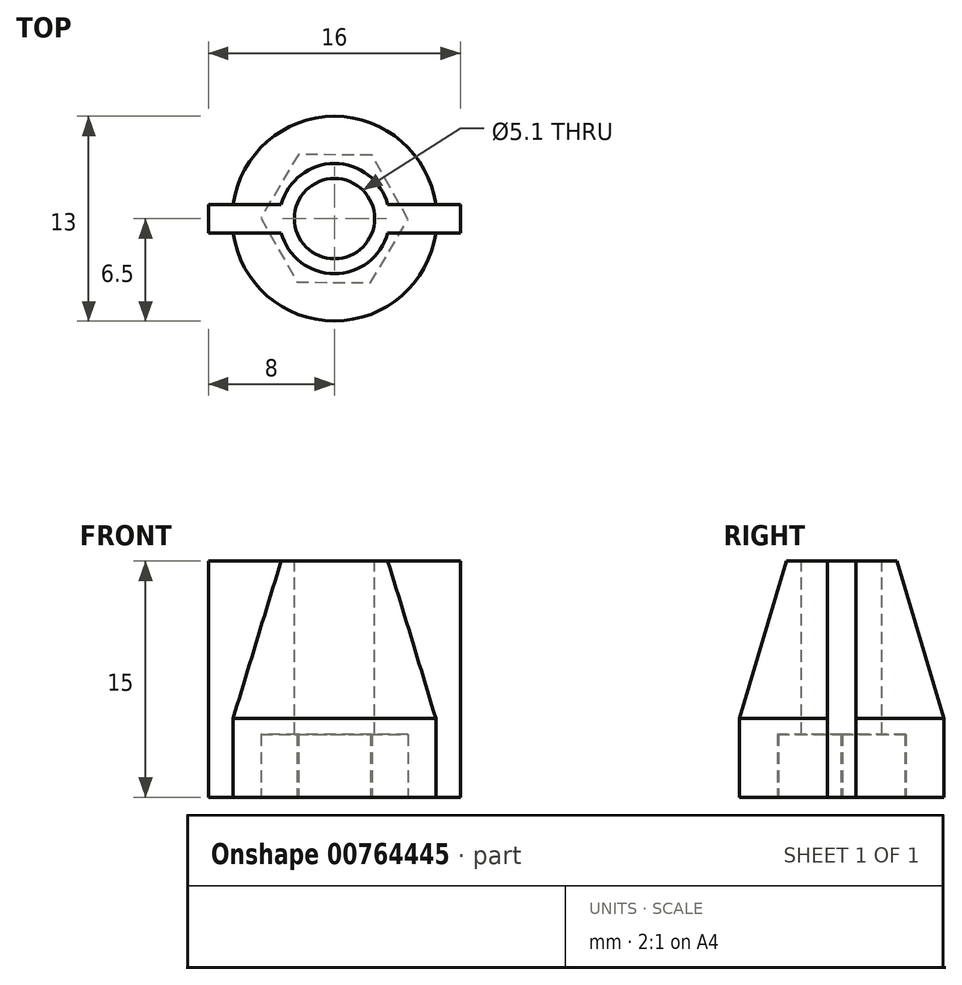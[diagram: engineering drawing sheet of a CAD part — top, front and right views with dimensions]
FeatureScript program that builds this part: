
annotation { "Feature Type Name" : "Feature", "Feature Type Description" : "" }
export const myFeature = defineFeature(function(context is Context, id is Id, definition is map)
    precondition{}
    {
        {
            var Q0;
            Q0=qCreatedBy(makeId("Top.planeOp"),FACE);
            var sketch = newSketch(context, id + "F0", { "sketchPlane" : qUnion([Q0])});
            skCircle(sketch, "E0", {"center": v(0, 0) * mm, "radius": 6.5 * mm});
            skSolve(sketch);
        }
        {
            var Q0;
            Q0 = qSketchRegion(id + "F0", true);
            extrude(context, id + "F1", {"entities" : qUnion([Q0]), "depth" : 15 * mm, "offsetDistance" : 25 * mm});
        }
        {
            var Q0;
            Q0=makeQuery(id+"F1.opExtrude","CAP_EDGE",EDGE,{"disambiguationData":[OSD([sQuery(id+"F0.wireOp",EDGE,"E0")])],"isStart":false});
            chamfer(context, id + "F2", {"entities" : qUnion([Q0]), "chamferType" : ChamferType.TWO_OFFSETS, "width1" : 3 * mm, "oppositeDirection" : false, "width2" : 10 * mm, "tangentPropagation" : true});
        }
        {
            var Q0;
            Q0=makeQuery(id+"F1.opExtrude","CAP_FACE",FACE,{"disambiguationData":[OSD([sQuery(id+"F0.wireOp",EDGE,"E0")])],"isStart":false});
            var sketch = newSketch(context, id + "F3", { "sketchPlane" : qUnion([Q0])});
            skLineSegment(sketch, "E1.bottom", {"start": v(8, 0.9) * mm, "end": v(-8, 0.9) * mm});
            skLineSegment(sketch, "E1.top", {"start": v(8, -0.9) * mm, "end": v(-8, -0.9) * mm});
            skLineSegment(sketch, "E1.left", {"start": v(8, 0.9) * mm, "end": v(8, -0.9) * mm});
            skLineSegment(sketch, "E1.right", {"start": v(-8, 0.9) * mm, "end": v(-8, -0.9) * mm});
            skPoint(sketch, "E1.middle", {"position": v(0, 0) * mm});
            skSolve(sketch);
        }
        {
            var Q0;
            Q0 = qSketchRegion(id + "F3", true);
            extrude(context, id + "F4", {"entities" : qUnion([Q0]), "operationType" : NewBodyOperationType.ADD, "oppositeDirection" : true, "depth" : 15 * mm, "offsetDistance" : 25 * mm});
        }
        {
            var Q0;
            Q0=makeQuery(id+"F4.boolean.opBoolean","MERGE",FACE,{"derivedFrom":[makeQuery(id+"F1.opExtrude","CAP_FACE",FACE,{"disambiguationData":[OSD([sQuery(id+"F0.wireOp",EDGE,"E0")])],"isStart":true}),makeQuery(id+"F4.opExtrude","CAP_FACE",FACE,{"disambiguationData":[OSD([sQuery(id+"F3.wireOp",EDGE,"E1.bottom"),sQuery(id+"F3.wireOp",EDGE,"E1.top"),sQuery(id+"F3.wireOp",EDGE,"E1.left"),sQuery(id+"F3.wireOp",EDGE,"E1.right")])],"isStart":false})]});
            var sketch = newSketch(context, id + "F5", { "sketchPlane" : qUnion([Q0])});
            skCircle(sketch, "E2.cCircle", {"center": v(0, 0) * mm, "radius": 4.05 * mm, "construction": true});
            skLineSegment(sketch, "E2.0", {"start": v(4.68, 0.05) * mm, "end": v(2.38, -4.03) * mm});
            skLineSegment(sketch, "E2.1", {"start": v(2.38, -4.03) * mm, "end": v(-2.3, -4.07) * mm});
            skLineSegment(sketch, "E2.2", {"start": v(-2.3, -4.07) * mm, "end": v(-4.68, -0.05) * mm});
            skLineSegment(sketch, "E2.3", {"start": v(-4.68, -0.05) * mm, "end": v(-2.38, 4.03) * mm});
            skLineSegment(sketch, "E2.4", {"start": v(-2.38, 4.03) * mm, "end": v(2.3, 4.07) * mm});
            skLineSegment(sketch, "E2.5", {"start": v(2.3, 4.07) * mm, "end": v(4.68, 0.05) * mm});
            skPoint(sketch, "E2.0.midPoint", {"position": v(3.53, -1.99) * mm});
            skSolve(sketch);
        }
        {
            var Q0;
            Q0 = qSketchRegion(id + "F5", true);
            extrude(context, id + "F6", {"entities" : qUnion([Q0]), "operationType" : NewBodyOperationType.REMOVE, "oppositeDirection" : true, "depth" : 4 * mm, "offsetDistance" : 25 * mm});
        }
        {
            var Q0;
            Q0=makeQuery(id+"F4.boolean.opBoolean","MERGE",FACE,{"derivedFrom":[makeQuery(id+"F1.opExtrude","CAP_FACE",FACE,{"disambiguationData":[OSD([sQuery(id+"F0.wireOp",EDGE,"E0")])],"isStart":false}),makeQuery(id+"F4.opExtrude","CAP_FACE",FACE,{"disambiguationData":[OSD([sQuery(id+"F3.wireOp",EDGE,"E1.bottom"),sQuery(id+"F3.wireOp",EDGE,"E1.top"),sQuery(id+"F3.wireOp",EDGE,"E1.left"),sQuery(id+"F3.wireOp",EDGE,"E1.right")])],"isStart":true})]});
            var sketch = newSketch(context, id + "F7", { "sketchPlane" : qUnion([Q0])});
            skCircle(sketch, "E3", {"center": v(0, 0) * mm, "radius": 2.55 * mm});
            skSolve(sketch);
        }
        {
            var Q0;
            Q0 = qSketchRegion(id + "F7", true);
            extrude(context, id + "F8", {"entities" : qUnion([Q0]), "operationType" : NewBodyOperationType.REMOVE, "oppositeDirection" : true, "depth" : 25 * mm, "offsetDistance" : 25 * mm});
        }
    });
